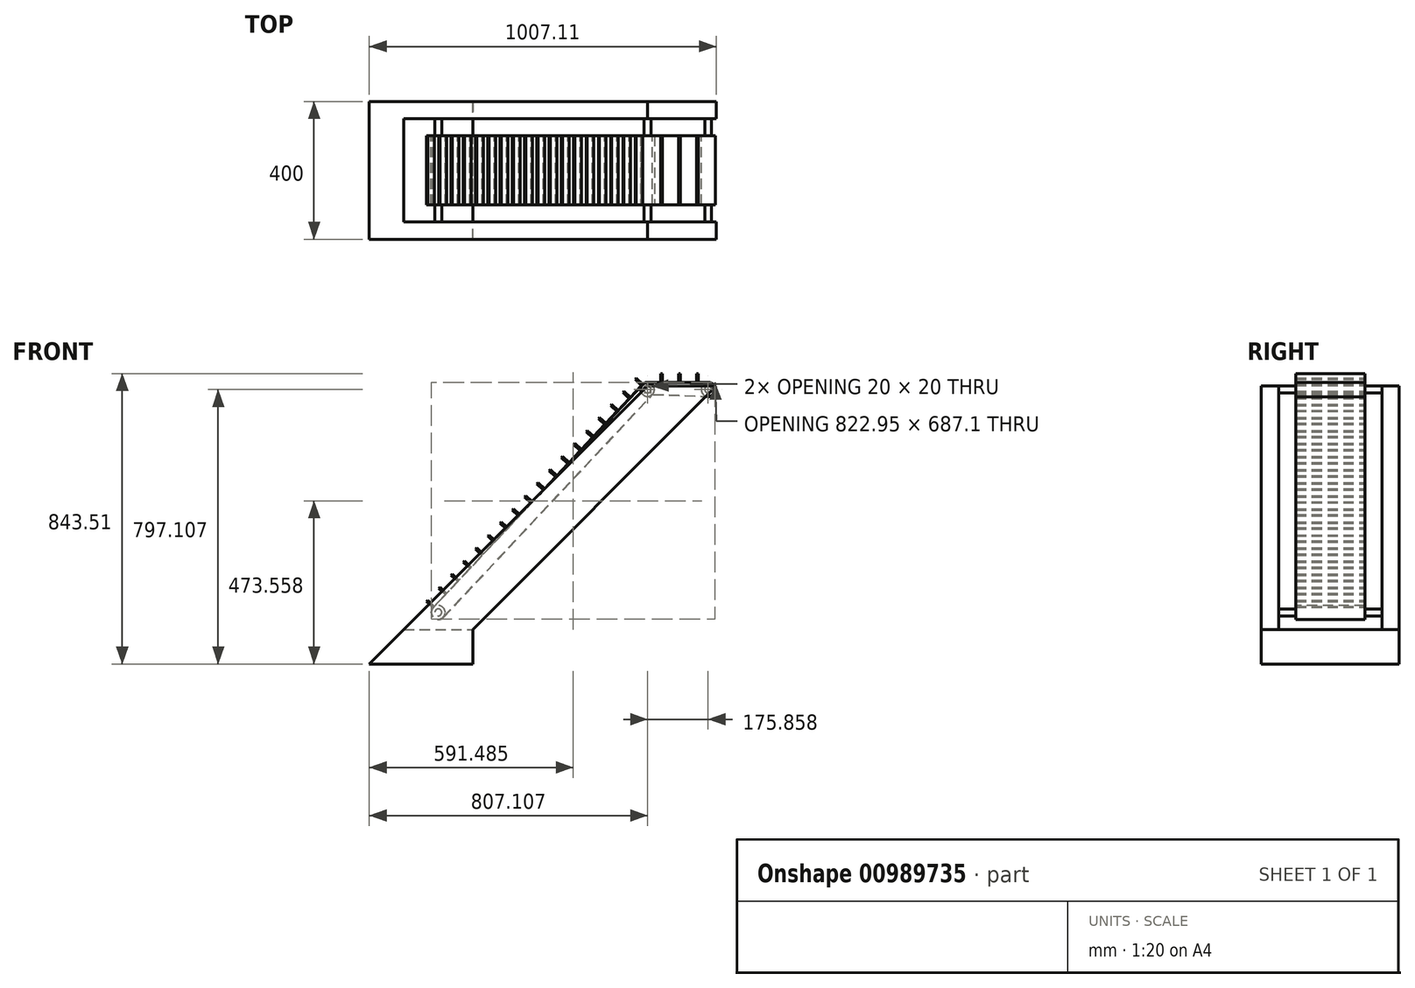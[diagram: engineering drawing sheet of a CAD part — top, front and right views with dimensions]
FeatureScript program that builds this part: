
annotation { "Feature Type Name" : "Feature", "Feature Type Description" : "" }
export const myFeature = defineFeature(function(context is Context, id is Id, definition is map)
    precondition{}
    {
        {
            var Q0;
            Q0=qCreatedBy(makeId("Front.planeOp"),FACE);
            var sketch = newSketch(context, id + "F0", { "sketchPlane" : qUnion([Q0])});
            skLineSegment(sketch, "E0", {"start": v(0, 0) * mm, "end": v(-300, 0) * mm});
            skLineSegment(sketch, "E1", {"start": v(-300, 0) * mm, "end": v(0, 300) * mm});
            skLineSegment(sketch, "E2", {"start": v(0, 300) * mm, "end": v(0, 0) * mm});
            skSolve(sketch);
        }
        {
            var Q0;
            Q0 = qSketchRegion(id + "F0", true);
            extrude(context, id + "F1", {"entities" : qUnion([Q0]), "endBound" : BoundingType.SYMMETRIC, "depth" : 400 * mm, "offsetDistance" : 25.4 * mm});
        }
        {
            var Q0;
            Q0=makeQuery(id+"F1.opExtrude","SWEPT_FACE",FACE,{"disambiguationData":[OSD([sQuery(id+"F0.wireOp",EDGE,"E2")])]});
            var sketch = newSketch(context, id + "F2", { "sketchPlane" : qUnion([Q0])});
            skLineSegment(sketch, "E3.bottom", {"start": v(-150, 300) * mm, "end": v(150, 300) * mm});
            skLineSegment(sketch, "E3.top", {"start": v(-150, 100) * mm, "end": v(150, 100) * mm});
            skLineSegment(sketch, "E3.left", {"start": v(-150, 300) * mm, "end": v(-150, 100) * mm});
            skLineSegment(sketch, "E3.right", {"start": v(150, 300) * mm, "end": v(150, 100) * mm});
            skLineSegment(sketch, "E4", {"start": v(0, 0) * mm, "end": v(0, 333.2) * mm, "construction": true});
            skSolve(sketch);
        }
        {
            var Q0;
            Q0 = qSketchRegion(id + "F2", true);
            extrude(context, id + "F3", {"entities" : qUnion([Q0]), "operationType" : NewBodyOperationType.REMOVE, "oppositeDirection" : true, "depth" : 228.6 * mm, "offsetDistance" : 25.4 * mm});
        }
        {
            var Q0;
            Q0=makeQuery(id+"F3.boolean.opBoolean","COPY",FACE,{"derivedFrom":makeQuery(id+"F3.opExtrude","SWEPT_FACE",FACE,{"disambiguationData":[OSD([sQuery(id+"F2.wireOp",EDGE,"E3.right")])]})});
            var sketch = newSketch(context, id + "F4", { "sketchPlane" : qUnion([Q0])});
            skLineSegment(sketch, "E5", {"start": v(0, 100) * mm, "end": v(707.1, 807.1) * mm});
            skLineSegment(sketch, "E6", {"start": v(0, 100) * mm, "end": v(0, 300) * mm});
            skLineSegment(sketch, "E7", {"start": v(0, 300) * mm, "end": v(507.1, 807.1) * mm});
            skLineSegment(sketch, "E8", {"start": v(507.1, 807.1) * mm, "end": v(707.1, 807.1) * mm});
            skSolve(sketch);
        }
        {
            var Q0;
            Q0 = qSketchRegion(id + "F4", true);
            var Q1;
            Q1=makeQuery(id+"F1.opExtrude","CAP_FACE",FACE,{"disambiguationData":[OSD([sQuery(id+"F0.wireOp",EDGE,"E0"),sQuery(id+"F0.wireOp",EDGE,"E1"),sQuery(id+"F0.wireOp",EDGE,"E2")])],"isStart":true});
            extrude(context, id + "F5", {"entities" : qUnion([Q0]), "operationType" : NewBodyOperationType.ADD, "endBound" : BoundingType.UP_TO_SURFACE, "oppositeDirection" : true, "depth" : 25.4 * mm, "endBoundEntityFace" : qUnion([Q1]), "offsetDistance" : 25.4 * mm});
        }
        {
            var Q0;
            Q0=makeQuery(id+"F3.boolean.opBoolean","COPY",FACE,{"derivedFrom":makeQuery(id+"F3.opExtrude","SWEPT_FACE",FACE,{"disambiguationData":[OSD([sQuery(id+"F2.wireOp",EDGE,"E3.left")])]})});
            var sketch = newSketch(context, id + "F6", { "sketchPlane" : qUnion([Q0])});
            skLineSegment(sketch, "E9", {"start": v(0, 100) * mm, "end": v(-707.1, 807.1) * mm});
            skLineSegment(sketch, "E10", {"start": v(0, 100) * mm, "end": v(0, 300) * mm});
            skLineSegment(sketch, "E11", {"start": v(0, 300) * mm, "end": v(-507.1, 807.1) * mm});
            skLineSegment(sketch, "E12", {"start": v(-707.1, 807.1) * mm, "end": v(-507.1, 807.1) * mm});
            skSolve(sketch);
        }
        {
            var Q0;
            Q0 = qSketchRegion(id + "F6", true);
            var Q1;
            Q1=makeQuery(id+"F1.opExtrude","CAP_FACE",FACE,{"disambiguationData":[OSD([sQuery(id+"F0.wireOp",EDGE,"E0"),sQuery(id+"F0.wireOp",EDGE,"E1"),sQuery(id+"F0.wireOp",EDGE,"E2")])],"isStart":false});
            extrude(context, id + "F7", {"entities" : qUnion([Q0]), "operationType" : NewBodyOperationType.ADD, "endBound" : BoundingType.UP_TO_SURFACE, "oppositeDirection" : true, "depth" : 25.4 * mm, "endBoundEntityFace" : qUnion([Q1]), "offsetDistance" : 25.4 * mm});
        }
        {
            var Q0;
            Q0=qCreatedBy(makeId("Front.planeOp"),FACE);
            var sketch = newSketch(context, id + "F8", { "sketchPlane" : qUnion([Q0])});
            skCircle(sketch, "E13", {"center": v(682.96, 797.1) * mm, "radius": 10 * mm});
            skSolve(sketch);
        }
        {
            var Q0;
            Q0 = qSketchRegion(id + "F8", true);
            extrude(context, id + "F9", {"entities" : qUnion([Q0]), "operationType" : NewBodyOperationType.ADD, "endBound" : BoundingType.SYMMETRIC, "depth" : 300 * mm, "offsetDistance" : 25.4 * mm});
        }
        {
            var Q0;
            Q0=qCreatedBy(makeId("Front.planeOp"),FACE);
            var sketch = newSketch(context, id + "F10", { "sketchPlane" : qUnion([Q0])});
            skCircle(sketch, "E14", {"center": v(682.96, 797.1) * mm, "radius": 20 * mm});
            skSolve(sketch);
        }
        {
            var Q0;
            Q0 = qSketchRegion(id + "F10", true);
            extrude(context, id + "F11", {"entities" : qUnion([Q0]), "operationType" : NewBodyOperationType.ADD, "endBound" : BoundingType.SYMMETRIC, "depth" : 200 * mm, "offsetDistance" : 25.4 * mm});
        }
        {
            var Q0;
            Q0=qCreatedBy(makeId("Front.planeOp"),FACE);
            var sketch = newSketch(context, id + "F12", { "sketchPlane" : qUnion([Q0])});
            skCircle(sketch, "E15", {"center": v(-100, 150) * mm, "radius": 10 * mm});
            skCircle(sketch, "E16", {"center": v(507.1, 797.1) * mm, "radius": 10 * mm});
            skSolve(sketch);
        }
        {
            var Q0;
            Q0 = qSketchRegion(id + "F12", true);
            extrude(context, id + "F13", {"entities" : qUnion([Q0]), "operationType" : NewBodyOperationType.ADD, "endBound" : BoundingType.SYMMETRIC, "depth" : 300 * mm, "offsetDistance" : 25.4 * mm});
        }
        {
            var Q0;
            Q0=qCreatedBy(makeId("Front.planeOp"),FACE);
            var sketch = newSketch(context, id + "F14", { "sketchPlane" : qUnion([Q0])});
            skCircle(sketch, "E17", {"center": v(-100, 150) * mm, "radius": 20 * mm});
            skCircle(sketch, "E18", {"center": v(507.1, 797.1) * mm, "radius": 20 * mm});
            skSolve(sketch);
        }
        {
            var Q0;
            Q0 = qSketchRegion(id + "F14", true);
            extrude(context, id + "F15", {"entities" : qUnion([Q0]), "operationType" : NewBodyOperationType.ADD, "endBound" : BoundingType.SYMMETRIC, "oppositeDirection" : true, "depth" : 200 * mm, "offsetDistance" : 25.4 * mm});
        }
        {
            var Q0;
            Q0=qCreatedBy(makeId("Front.planeOp"),FACE);
            var sketch = newSketch(context, id + "F16", { "sketchPlane" : qUnion([Q0])});
            skArc(sketch, "E19", {"start": v(-114.59, 163.68) * mm, "mid": v(-113.68, 135.41) * mm, "end": v(-85.41, 136.32) * mm});
            skArc(sketch, "E20", {"start": v(-115.32, 164.37) * mm, "mid": v(-114.37, 134.68) * mm, "end": v(-84.68, 135.63) * mm});
            skArc(sketch, "E21", {"start": v(521.7, 783.42) * mm, "mid": v(492.74, 811.02) * mm, "end": v(521.25, 782.97) * mm});
            skArc(sketch, "E22", {"start": v(507.1, 818.1) * mm, "mid": v(498.76, 816.38) * mm, "end": v(491.8, 811.48) * mm});
            skLineSegment(sketch, "E23", {"start": v(491.8, 811.48) * mm, "end": v(-115.32, 164.37) * mm});
            skLineSegment(sketch, "E24", {"start": v(-84.68, 135.63) * mm, "end": v(521.63, 781.9) * mm});
            skLineSegment(sketch, "E25", {"start": v(492.52, 810.8) * mm, "end": v(-114.59, 163.68) * mm});
            skLineSegment(sketch, "E26", {"start": v(-85.41, 136.32) * mm, "end": v(521.7, 783.42) * mm});
            skCircle(sketch, "E27", {"center": v(682.96, 797.1) * mm, "radius": 20 * mm});
            skArc(sketch, "E28", {"start": v(682.1, 776.12) * mm, "mid": v(703.96, 796.67) * mm, "end": v(682.96, 818.1) * mm});
            skLineSegment(sketch, "E29", {"start": v(507.1, 818.1) * mm, "end": v(682.96, 818.1) * mm});
            skLineSegment(sketch, "E30", {"start": v(523.58, 782.7) * mm, "end": v(682.1, 776.12) * mm});
            skLineSegment(sketch, "E31", {"start": v(507.1, 817.1) * mm, "end": v(682.96, 817.1) * mm});
            skLineSegment(sketch, "E32", {"start": v(523.15, 783.7) * mm, "end": v(682.14, 777.12) * mm});
            skArc(sketch, "E33.trimOffspring", {"start": v(507.1, 817.1) * mm, "mid": v(499.16, 815.46) * mm, "end": v(492.52, 810.8) * mm});
            skPoint(sketch, "E34.visualSharp", {"position": v(522, 783.76) * mm});
            skArc(sketch, "E34.filletArc", {"start": v(523.15, 783.7) * mm, "mid": v(522.12, 783.54) * mm, "end": v(521.25, 782.97) * mm});
            skPoint(sketch, "E35.visualSharp", {"position": v(522.42, 782.74) * mm});
            skArc(sketch, "E35.filletArc", {"start": v(523.58, 782.7) * mm, "mid": v(522.52, 782.5) * mm, "end": v(521.63, 781.9) * mm});
            skSolve(sketch);
        }
        {
            var Q0;
            Q0 = qSketchRegion(id + "F16", true);
            extrude(context, id + "F17", {"entities" : qUnion([Q0]), "endBound" : BoundingType.SYMMETRIC, "depth" : 200 * mm, "offsetDistance" : 25.4 * mm});
        }
        {
            var Q0;
            Q0=makeQuery(id+"F17.opExtrude","SWEPT_FACE",FACE,{"disambiguationData":[OSD([sQuery(id+"F16.wireOp",EDGE,"E23")])]});
            var sketch = newSketch(context, id + "F18", { "sketchPlane" : qUnion([Q0])});
            skLineSegment(sketch, "E36.bottom", {"start": v(100, 40.97) * mm, "end": v(-100, 40.97) * mm});
            skLineSegment(sketch, "E36.top", {"start": v(100, 45.97) * mm, "end": v(-100, 45.97) * mm});
            skLineSegment(sketch, "E36.left", {"start": v(100, 40.97) * mm, "end": v(100, 45.97) * mm});
            skLineSegment(sketch, "E36.right", {"start": v(-100, 40.97) * mm, "end": v(-100, 45.97) * mm});
            skLineSegment(sketch, "E37.0.1.0", {"start": v(100, 97.97) * mm, "end": v(-100, 97.97) * mm});
            skLineSegment(sketch, "E37.0.1.1", {"start": v(100, 92.97) * mm, "end": v(-100, 92.97) * mm});
            skLineSegment(sketch, "E37.0.1.2", {"start": v(-100, 92.97) * mm, "end": v(-100, 97.97) * mm});
            skLineSegment(sketch, "E37.0.1.3", {"start": v(100, 92.97) * mm, "end": v(100, 97.97) * mm});
            skLineSegment(sketch, "E37.0.2.0", {"start": v(100, 149.97) * mm, "end": v(-100, 149.97) * mm});
            skLineSegment(sketch, "E37.0.2.1", {"start": v(100, 144.97) * mm, "end": v(-100, 144.97) * mm});
            skLineSegment(sketch, "E37.0.2.2", {"start": v(-100, 144.97) * mm, "end": v(-100, 149.97) * mm});
            skLineSegment(sketch, "E37.0.2.3", {"start": v(100, 144.97) * mm, "end": v(100, 149.97) * mm});
            skLineSegment(sketch, "E37.0.3.0", {"start": v(100, 201.97) * mm, "end": v(-100, 201.97) * mm});
            skLineSegment(sketch, "E37.0.3.1", {"start": v(100, 196.97) * mm, "end": v(-100, 196.97) * mm});
            skLineSegment(sketch, "E37.0.3.2", {"start": v(-100, 196.97) * mm, "end": v(-100, 201.97) * mm});
            skLineSegment(sketch, "E37.0.3.3", {"start": v(100, 196.97) * mm, "end": v(100, 201.97) * mm});
            skLineSegment(sketch, "E37.0.4.0", {"start": v(100, 253.97) * mm, "end": v(-100, 253.97) * mm});
            skLineSegment(sketch, "E37.0.4.1", {"start": v(100, 248.97) * mm, "end": v(-100, 248.97) * mm});
            skLineSegment(sketch, "E37.0.4.2", {"start": v(-100, 248.97) * mm, "end": v(-100, 253.97) * mm});
            skLineSegment(sketch, "E37.0.4.3", {"start": v(100, 248.97) * mm, "end": v(100, 253.97) * mm});
            skLineSegment(sketch, "E37.0.5.0", {"start": v(100, 305.97) * mm, "end": v(-100, 305.97) * mm});
            skLineSegment(sketch, "E37.0.5.1", {"start": v(100, 300.97) * mm, "end": v(-100, 300.97) * mm});
            skLineSegment(sketch, "E37.0.5.2", {"start": v(-100, 300.97) * mm, "end": v(-100, 305.97) * mm});
            skLineSegment(sketch, "E37.0.5.3", {"start": v(100, 300.97) * mm, "end": v(100, 305.97) * mm});
            skLineSegment(sketch, "E37.0.6.0", {"start": v(100, 357.97) * mm, "end": v(-100, 357.97) * mm});
            skLineSegment(sketch, "E37.0.6.1", {"start": v(100, 352.97) * mm, "end": v(-100, 352.97) * mm});
            skLineSegment(sketch, "E37.0.6.2", {"start": v(-100, 352.97) * mm, "end": v(-100, 357.97) * mm});
            skLineSegment(sketch, "E37.0.6.3", {"start": v(100, 352.97) * mm, "end": v(100, 357.97) * mm});
            skLineSegment(sketch, "E37.0.7.0", {"start": v(100, 409.97) * mm, "end": v(-100, 409.97) * mm});
            skLineSegment(sketch, "E37.0.7.1", {"start": v(100, 404.97) * mm, "end": v(-100, 404.97) * mm});
            skLineSegment(sketch, "E37.0.7.2", {"start": v(-100, 404.97) * mm, "end": v(-100, 409.97) * mm});
            skLineSegment(sketch, "E37.0.7.3", {"start": v(100, 404.97) * mm, "end": v(100, 409.97) * mm});
            skLineSegment(sketch, "E37.0.8.0", {"start": v(100, 461.97) * mm, "end": v(-100, 461.97) * mm});
            skLineSegment(sketch, "E37.0.8.1", {"start": v(100, 456.97) * mm, "end": v(-100, 456.97) * mm});
            skLineSegment(sketch, "E37.0.8.2", {"start": v(-100, 456.97) * mm, "end": v(-100, 461.97) * mm});
            skLineSegment(sketch, "E37.0.8.3", {"start": v(100, 456.97) * mm, "end": v(100, 461.97) * mm});
            skLineSegment(sketch, "E37.0.9.0", {"start": v(100, 513.97) * mm, "end": v(-100, 513.97) * mm});
            skLineSegment(sketch, "E37.0.9.1", {"start": v(100, 508.97) * mm, "end": v(-100, 508.97) * mm});
            skLineSegment(sketch, "E37.0.9.2", {"start": v(-100, 508.97) * mm, "end": v(-100, 513.97) * mm});
            skLineSegment(sketch, "E37.0.9.3", {"start": v(100, 508.97) * mm, "end": v(100, 513.97) * mm});
            skLineSegment(sketch, "E37.0.10.0", {"start": v(100, 565.97) * mm, "end": v(-100, 565.97) * mm});
            skLineSegment(sketch, "E37.0.10.1", {"start": v(100, 560.97) * mm, "end": v(-100, 560.97) * mm});
            skLineSegment(sketch, "E37.0.10.2", {"start": v(-100, 560.97) * mm, "end": v(-100, 565.97) * mm});
            skLineSegment(sketch, "E37.0.10.3", {"start": v(100, 560.97) * mm, "end": v(100, 565.97) * mm});
            skLineSegment(sketch, "E37.0.11.0", {"start": v(100, 617.97) * mm, "end": v(-100, 617.97) * mm});
            skLineSegment(sketch, "E37.0.11.1", {"start": v(100, 612.97) * mm, "end": v(-100, 612.97) * mm});
            skLineSegment(sketch, "E37.0.11.2", {"start": v(-100, 612.97) * mm, "end": v(-100, 617.97) * mm});
            skLineSegment(sketch, "E37.0.11.3", {"start": v(100, 612.97) * mm, "end": v(100, 617.97) * mm});
            skLineSegment(sketch, "E37.0.12.0", {"start": v(100, 669.97) * mm, "end": v(-100, 669.97) * mm});
            skLineSegment(sketch, "E37.0.12.1", {"start": v(100, 664.97) * mm, "end": v(-100, 664.97) * mm});
            skLineSegment(sketch, "E37.0.12.2", {"start": v(-100, 664.97) * mm, "end": v(-100, 669.97) * mm});
            skLineSegment(sketch, "E37.0.12.3", {"start": v(100, 664.97) * mm, "end": v(100, 669.97) * mm});
            skLineSegment(sketch, "E37.0.13.0", {"start": v(100, 721.97) * mm, "end": v(-100, 721.97) * mm});
            skLineSegment(sketch, "E37.0.13.1", {"start": v(100, 716.97) * mm, "end": v(-100, 716.97) * mm});
            skLineSegment(sketch, "E37.0.13.2", {"start": v(-100, 716.97) * mm, "end": v(-100, 721.97) * mm});
            skLineSegment(sketch, "E37.0.13.3", {"start": v(100, 716.97) * mm, "end": v(100, 721.97) * mm});
            skLineSegment(sketch, "E37.0.14.0", {"start": v(100, 773.97) * mm, "end": v(-100, 773.97) * mm});
            skLineSegment(sketch, "E37.0.14.1", {"start": v(100, 768.97) * mm, "end": v(-100, 768.97) * mm});
            skLineSegment(sketch, "E37.0.14.2", {"start": v(-100, 768.97) * mm, "end": v(-100, 773.97) * mm});
            skLineSegment(sketch, "E37.0.14.3", {"start": v(100, 768.97) * mm, "end": v(100, 773.97) * mm});
            skLineSegment(sketch, "E37.0.15.0", {"start": v(100, 825.97) * mm, "end": v(-100, 825.97) * mm});
            skLineSegment(sketch, "E37.0.15.1", {"start": v(100, 820.97) * mm, "end": v(-100, 820.97) * mm});
            skLineSegment(sketch, "E37.0.15.2", {"start": v(-100, 820.97) * mm, "end": v(-100, 825.97) * mm});
            skLineSegment(sketch, "E37.0.15.3", {"start": v(100, 820.97) * mm, "end": v(100, 825.97) * mm});
            skLineSegment(sketch, "E37.0.16.0", {"start": v(100, 877.97) * mm, "end": v(-100, 877.97) * mm});
            skLineSegment(sketch, "E37.0.16.1", {"start": v(100, 872.97) * mm, "end": v(-100, 872.97) * mm});
            skLineSegment(sketch, "E37.0.16.2", {"start": v(-100, 872.97) * mm, "end": v(-100, 877.97) * mm});
            skLineSegment(sketch, "E37.0.16.3", {"start": v(100, 872.97) * mm, "end": v(100, 877.97) * mm});
            skLineSegment(sketch, "E37.0.17.0", {"start": v(100, 929.97) * mm, "end": v(-100, 929.97) * mm});
            skLineSegment(sketch, "E37.0.17.1", {"start": v(100, 924.97) * mm, "end": v(-100, 924.97) * mm});
            skLineSegment(sketch, "E37.0.17.2", {"start": v(-100, 924.97) * mm, "end": v(-100, 929.97) * mm});
            skLineSegment(sketch, "E37.0.17.3", {"start": v(100, 924.97) * mm, "end": v(100, 929.97) * mm});
            skLineSegment(sketch, "E37.direction1", {"start": v(-100, 45.97) * mm, "end": v(-74.6, 45.97) * mm, "construction": true});
            skLineSegment(sketch, "E37.direction2", {"start": v(-100, 45.97) * mm, "end": v(-100, 97.97) * mm, "construction": true});
            skSolve(sketch);
        }
        {
            var Q0;
            Q0 = qSketchRegion(id + "F18", true);
            extrude(context, id + "F19", {"entities" : qUnion([Q0]), "operationType" : NewBodyOperationType.ADD, "depth" : 25.4 * mm, "offsetDistance" : 25.4 * mm});
        }
        {
            var Q0;
            Q0=makeQuery(id+"F17.opExtrude","SWEPT_FACE",FACE,{"disambiguationData":[OSD([sQuery(id+"F16.wireOp",EDGE,"E29")])]});
            var sketch = newSketch(context, id + "F20", { "sketchPlane" : qUnion([Q0])});
            skLineSegment(sketch, "E38.bottom", {"start": v(544.95, 100) * mm, "end": v(549.95, 100) * mm});
            skLineSegment(sketch, "E38.top", {"start": v(544.95, -100) * mm, "end": v(549.95, -100) * mm});
            skLineSegment(sketch, "E38.left", {"start": v(544.95, 100) * mm, "end": v(544.95, -100) * mm});
            skLineSegment(sketch, "E38.right", {"start": v(549.95, 100) * mm, "end": v(549.95, -100) * mm});
            skLineSegment(sketch, "E39.1.0.0", {"start": v(596.95, 100) * mm, "end": v(596.95, -100) * mm});
            skLineSegment(sketch, "E39.1.0.1", {"start": v(596.95, -100) * mm, "end": v(601.95, -100) * mm});
            skLineSegment(sketch, "E39.1.0.2", {"start": v(601.95, 100) * mm, "end": v(601.95, -100) * mm});
            skLineSegment(sketch, "E39.1.0.3", {"start": v(596.95, 100) * mm, "end": v(601.95, 100) * mm});
            skLineSegment(sketch, "E39.2.0.0", {"start": v(648.95, 100) * mm, "end": v(648.95, -100) * mm});
            skLineSegment(sketch, "E39.2.0.1", {"start": v(648.95, -100) * mm, "end": v(653.95, -100) * mm});
            skLineSegment(sketch, "E39.2.0.2", {"start": v(653.95, 100) * mm, "end": v(653.95, -100) * mm});
            skLineSegment(sketch, "E39.2.0.3", {"start": v(648.95, 100) * mm, "end": v(653.95, 100) * mm});
            skLineSegment(sketch, "E39.direction1", {"start": v(544.95, -100) * mm, "end": v(596.95, -100) * mm, "construction": true});
            skSolve(sketch);
        }
        {
            var Q0;
            Q0 = qSketchRegion(id + "F20", true);
            extrude(context, id + "F21", {"entities" : qUnion([Q0]), "operationType" : NewBodyOperationType.ADD, "depth" : 25.4 * mm, "offsetDistance" : 25.4 * mm});
        }
    });
